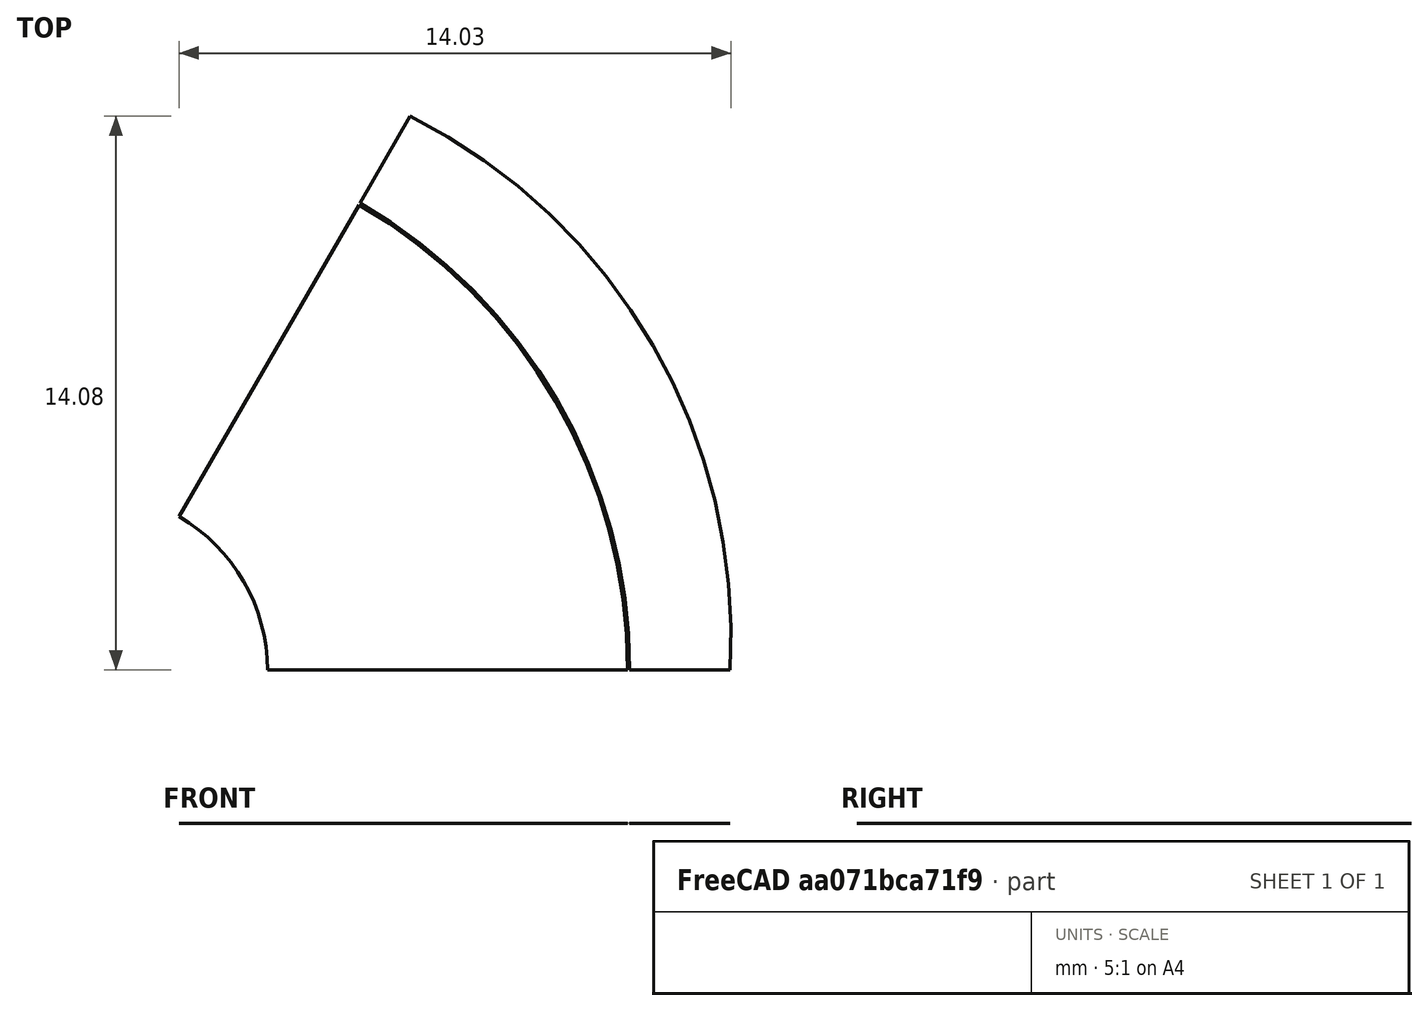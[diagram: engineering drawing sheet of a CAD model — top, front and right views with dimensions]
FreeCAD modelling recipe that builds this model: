
FCSTD DOCUMENT  (FreeCAD 0.18R4 (GitTag))
Label: RotorIRRingMagnet
License: All rights reserved
LicenseURL: http://en.wikipedia.org/wiki/All_rights_reserved
objects: Sketcher::SketchObject×5, PartDesign::Body×2, Surface::Filling×2, Spreadsheet::Sheet×1
note: 9 computed .brp shape members not serialized (recipe doc carries the construction recipe); baked Part::Feature solids carry a one-line shape summary decoded from their .brp

FEATURE [Spreadsheet::Sheet] Spreadsheet  label="Variables"
  cells = A2=poleNumber; B2(poleNumber)=6; A3=outerDiameter; B3(outerDiameter)=33; D3=Calc Value; A4=innerDiameter; B4(innerDiameter)=9; D4=Input Value; A5=stackLength; B5(stackLength)=20; A6=stackingFactor; B6(stackingFactor)=0.95; A7=embrace; B7(embrace)=75; A8=contourRatio; B8(contourRatio)=90; A9=magnetAirgap; B9(magnetAirgap)=0.05; A10=poleSeparation; B10(poleSeparation)=2; A11=magnetWidth; B11(magnetWidth)=9; A12=magnetHeight; B12(magnetHeight)=2.8; A13=rib; B13(rib)=0.5; A14=bridgeCurved; B14(bridgeCurved)=0.5; A15=cutTop; B15(cutTop)=0.2; A16=cutBottom; B16(cutBottom)=0.25; A17=segmentAngle; B17(segmentAngle)==360 / poleNumber; A18=movePocketInwards; B18(movePocketInwards)=0.5; A19=cuttingThickness; B19(cuttingThickness)=0.1; A20=magnetLength; B20(magnetLength)==stackLength; A21=cut; B21(cut)=0.2; A22=ribShaft; B22(ribShaft)=0.5; A23=magnetEmbrace; B23(magnetEmbrace)=70; A24=magnetContourRatio; B24(magnetContourRatio)=90; A25=axialMisalignment; B25(axialMisalignment)=0.5
FEATURE [Sketcher::SketchObject] Sketch003  label="RotorSketch"
  MapMode = 5
  Support = -> [XY_Plane]
  expr: Constraints[15] = Variables.outerDiameter / 2
  expr: Constraints[18] = Variables.segmentAngle / 2
  expr: Constraints[0] = Variables.segmentAngle
  expr: Constraints[27] = Variables.outerDiameter / 2 - Variables.magnetHeight - Variables.magnetAirgap
  expr: Constraints[14] = Variables.innerDiameter / 2
  expr: Constraints[23] = Variables.outerDiameter / 2 * Variables.contourRatio / 100
  sketch-geometry (11):
    g0: LineSegment [constr] StartX=4.5 StartY=0 StartZ=0 EndX=16.5 EndY=0 EndZ=0
    g1: LineSegment [constr] StartX=2.25 StartY=3.89711 StartZ=0 EndX=8.25 EndY=14.2894 EndZ=0
    g2: LineSegment [constr] StartX=0 StartY=0 StartZ=0 EndX=4.5 EndY=0 EndZ=0
    g3: LineSegment [constr] StartX=0 StartY=0 StartZ=0 EndX=2.25 EndY=3.89711 EndZ=0
    g4: ArcOfCircle [constr] CenterX=0 CenterY=0 CenterZ=0 NormalX=0 NormalY=0 NormalZ=1 AngleXU=0 Radius=16.5 StartAngle=0 EndAngle=1.0472
    g5: ArcOfCircle CenterX=0 CenterY=0 CenterZ=0 NormalX=0 NormalY=0 NormalZ=1 AngleXU=0 Radius=4.5 StartAngle=0 EndAngle=1.0472
    g6: LineSegment [constr] StartX=0 StartY=0 StartZ=0 EndX=14.2894 EndY=8.25 EndZ=0
    g7: ArcOfCircle [constr] CenterX=1.42894 CenterY=0.825 CenterZ=0 NormalX=0 NormalY=0 NormalZ=1 AngleXU=0 Radius=14.85 StartAngle=6.2276 EndAngle=7.38597
    g8: ArcOfCircle CenterX=0 CenterY=0 CenterZ=0 NormalX=0 NormalY=0 NormalZ=1 AngleXU=0 Radius=13.65 StartAngle=0 EndAngle=1.0472
    g9: LineSegment StartX=2.25 StartY=3.89711 StartZ=0 EndX=6.825 EndY=11.8212 EndZ=0
    g10: LineSegment StartX=4.5 StartY=0 StartZ=0 EndX=13.65 EndY=0 EndZ=0
  constraints (32):
    c: Angle(g0,g1) = 1.0472
    c: Coincident(g2,g-1)
    c: Coincident(g2,g0)
    c: Coincident(g3,g2)
    c: Coincident(g3,g1)
    c: Parallel(g2,g0)
    c: Parallel(g3,g1)
    c: Coincident(g4,g-1)
    c: Coincident(g4,g0)
    c: Coincident(g4,g1)
    c: Coincident(g5,g4)
    c: Coincident(g5,g1)
    c: Coincident(g5,g0)
    c: Angle(g-1,g2) = 0
    c: Radius(g5) = 4.5
    c: Radius(g4) = 16.5
    c: Coincident(g6,g5)
    c: PointOnObject(g6,g4)
    c: Angle(g-1,g6) = 0.523599
    c: PointOnObject(g7,g1)
    c: PointOnObject(g7,g0)
    c: PointOnObject(g6,g7)
    c: PointOnObject(g7,g6)
    c: Radius(g7) = 14.85
    c: Coincident(g8,g5)
    c: PointOnObject(g8,g1)
    c: PointOnObject(g8,g0)
    c: Radius(g8) = 13.65
    c: Coincident(g9,g5)
    c: Coincident(g9,g8)
    c: Coincident(g10,g5)
    c: Coincident(g10,g8)
FEATURE [Sketcher::SketchObject] Sketch004  label="BoundingBox"
  MapMode = 5
  Support = -> [XY_Plane]
  expr: Constraints[8] = Variables.outerDiameter
  sketch-geometry (6):
    g0: LineSegment StartX=-16.5 StartY=-16.5 StartZ=0 EndX=16.5 EndY=-16.5 EndZ=0
    g1: LineSegment StartX=16.5 StartY=-16.5 StartZ=0 EndX=16.5 EndY=16.5 EndZ=0
    g2: LineSegment StartX=16.5 StartY=16.5 StartZ=0 EndX=-16.5 EndY=16.5 EndZ=0
    g3: LineSegment StartX=-16.5 StartY=16.5 StartZ=0 EndX=-16.5 EndY=-16.5 EndZ=0
    g4: LineSegment [constr] StartX=-16.5 StartY=-16.5 StartZ=0 EndX=16.5 EndY=16.5 EndZ=0
    g5: GeomPoint X=0 Y=0 Z=0
  constraints (14):
    c: Coincident(g0,g1)
    c: Coincident(g1,g2)
    c: Coincident(g2,g3)
    c: Coincident(g3,g0)
    c: Horizontal(g0)
    c: Horizontal(g2)
    c: Vertical(g1)
    c: Vertical(g3)
    c: DistanceY(g1,g1) = 33
    c: Equal(g2,g1)
    c: Coincident(g4,g0)
    c: Coincident(g4,g1)
    c: Symmetric(g0,g1,g5)
    c: Coincident(g-1,g5)
FEATURE [Sketcher::SketchObject] Sketch005  label="RotorSideSketch"
  MapMode = 5
  Support = -> [XY_Plane001]
  expr: Constraints[22] = Variables.stackLength / 2 - Variables.axialMisalignment
  expr: Constraints[9] = Variables.outerDiameter / 2
  expr: Constraints[8] = Variables.innerDiameter / 2
  expr: Constraints[7] = Variables.stackLength
  sketch-geometry (8):
    g0: LineSegment StartX=-9.5 StartY=4.5 StartZ=0 EndX=10.5 EndY=4.5 EndZ=0
    g1: LineSegment StartX=10.5 StartY=4.5 StartZ=0 EndX=10.5 EndY=16.5 EndZ=0
    g2: LineSegment StartX=10.5 StartY=16.5 StartZ=0 EndX=-9.5 EndY=16.5 EndZ=0
    g3: LineSegment StartX=-9.5 StartY=16.5 StartZ=0 EndX=-9.5 EndY=4.5 EndZ=0
    g4: LineSegment StartX=-9.5 StartY=-4.5 StartZ=0 EndX=10.5 EndY=-4.5 EndZ=0
    g5: LineSegment StartX=10.5 StartY=-4.5 StartZ=0 EndX=10.5 EndY=-16.5 EndZ=0
    g6: LineSegment StartX=10.5 StartY=-16.5 StartZ=0 EndX=-9.5 EndY=-16.5 EndZ=0
    g7: LineSegment StartX=-9.5 StartY=-16.5 StartZ=0 EndX=-9.5 EndY=-4.5 EndZ=0
  constraints (23):
    c: Coincident(g0,g1)
    c: Coincident(g1,g2)
    c: Coincident(g2,g3)
    c: Coincident(g3,g0)
    c: Horizontal(g0)
    c: Vertical(g1)
    c: Vertical(g3)
    c: DistanceX(g2,g2) = 20
    c: DistanceY(g-1,g0) = 4.5
    c: DistanceY(g-1,g1) = 16.5
    c: Coincident(g4,g5)
    c: Coincident(g5,g6)
    c: Coincident(g6,g7)
    c: Coincident(g7,g4)
    c: Horizontal(g4)
    c: Vertical(g5)
    c: Vertical(g7)
    c: Equal(g4,g0)
    c: Equal(g7,g3)
    c: Horizontal(g6)
    c: Horizontal(g2)
    c: Symmetric(g4,g0,g-1)
    c: DistanceX(g0,g-1) = 9.5
FEATURE [Sketcher::SketchObject] Sketch006  label="MagnetSideSketch"
  ExternalGeometry = -> [Sketch005]
  MapMode = 5
  Support = -> [XY_Plane001]
  expr: Constraints[19] = Variables.stackLength / 2 - Variables.axialMisalignment
  expr: Constraints[7] = Variables.magnetHeight
  sketch-geometry (8):
    g0: LineSegment StartX=-9.5 StartY=13.7 StartZ=0 EndX=10.5 EndY=13.7 EndZ=0
    g1: LineSegment StartX=10.5 StartY=13.7 StartZ=0 EndX=10.5 EndY=16.5 EndZ=0
    g2: LineSegment StartX=10.5 StartY=16.5 StartZ=0 EndX=-9.5 EndY=16.5 EndZ=0
    g3: LineSegment StartX=-9.5 StartY=16.5 StartZ=0 EndX=-9.5 EndY=13.7 EndZ=0
    g4: LineSegment StartX=-9.5 StartY=-16.5 StartZ=0 EndX=10.5 EndY=-16.5 EndZ=0
    g5: LineSegment StartX=10.5 StartY=-16.5 StartZ=0 EndX=10.5 EndY=-13.7 EndZ=0
    g6: LineSegment StartX=10.5 StartY=-13.7 StartZ=0 EndX=-9.5 EndY=-13.7 EndZ=0
    g7: LineSegment StartX=-9.5 StartY=-13.7 StartZ=0 EndX=-9.5 EndY=-16.5 EndZ=0
  constraints (21):
    c: Coincident(g0,g1)
    c: Coincident(g1,g2)
    c: Coincident(g2,g3)
    c: Coincident(g3,g0)
    c: Horizontal(g0)
    c: Vertical(g1)
    c: Vertical(g3)
    c: DistanceY(g1,g1) = 2.8
    c: Coincident(g4,g5)
    c: Coincident(g5,g6)
    c: Coincident(g6,g7)
    c: Coincident(g7,g4)
    c: Horizontal(g4)
    c: Vertical(g5)
    c: Vertical(g7)
    c: Symmetric(g6,g0,g-1)
    c: Symmetric(g5,g0,g-1)
    c: Equal(g7,g3)
    c: Coincident(g1,g-3)
    c: DistanceX(g0,g-1) = 9.5
    c: Horizontal(g2)
FEATURE [PartDesign::Body] Body001  label="SideView"
  Group = -> [Sketch005,Sketch006]
  Origin = -> Origin001
FEATURE [Surface::Filling] Surface  label="Rotor_Surface"
  Anisotropy = false
  BoundaryEdges = -> [Sketch003]
  BoundaryOrder = [0,0,0,0]
  Degree = 3
  Iterations = 2
  MaximumDegree = 8
  MaximumSegments = 9
  PointsOnCurve = 15
  TolAngular = 0.01
  TolCurvature = 0.1
  Tolerance2d = 1e-05
  Tolerance3d = 0.0001
FEATURE [Sketcher::SketchObject] Sketch007  label="MagnetSketch"
  MapMode = 5
  Support = -> [XY_Plane]
  expr: Constraints[35] = Variables.outerDiameter / 2 - Variables.magnetHeight
  expr: Constraints[15] = Variables.outerDiameter / 2
  expr: Constraints[18] = Variables.segmentAngle / 2
  expr: Constraints[0] = Variables.segmentAngle
  expr: Constraints[27] = Variables.outerDiameter / 2 - Variables.magnetHeight - Variables.magnetAirgap
  expr: Constraints[14] = Variables.innerDiameter / 2
  expr: Constraints[23] = Variables.outerDiameter / 2 * Variables.magnetContourRatio / 100
  sketch-geometry (14):
    g0: LineSegment [constr] StartX=4.5 StartY=0 StartZ=0 EndX=16.5 EndY=0 EndZ=0
    g1: LineSegment [constr] StartX=2.25 StartY=3.89711 StartZ=0 EndX=8.25 EndY=14.2894 EndZ=0
    g2: LineSegment [constr] StartX=0 StartY=0 StartZ=0 EndX=4.5 EndY=0 EndZ=0
    g3: LineSegment [constr] StartX=0 StartY=0 StartZ=0 EndX=2.25 EndY=3.89711 EndZ=0
    g4: ArcOfCircle [constr] CenterX=0 CenterY=0 CenterZ=0 NormalX=0 NormalY=0 NormalZ=1 AngleXU=0 Radius=16.5 StartAngle=0 EndAngle=1.0472
    g5: ArcOfCircle [constr] CenterX=0 CenterY=0 CenterZ=0 NormalX=0 NormalY=0 NormalZ=1 AngleXU=0 Radius=4.5 StartAngle=0 EndAngle=1.0472
    g6: LineSegment [constr] StartX=0 StartY=0 StartZ=0 EndX=14.2894 EndY=8.25 EndZ=0
    g7: ArcOfCircle CenterX=1.42894 CenterY=0.825 CenterZ=0 NormalX=0 NormalY=0 NormalZ=1 AngleXU=0 Radius=14.85 StartAngle=6.2276 EndAngle=7.38597
    g8: ArcOfCircle [constr] CenterX=0 CenterY=0 CenterZ=0 NormalX=0 NormalY=0 NormalZ=1 AngleXU=0 Radius=13.65 StartAngle=0 EndAngle=1.0472
    g9: LineSegment [constr] StartX=2.25 StartY=3.89711 StartZ=0 EndX=6.825 EndY=11.8212 EndZ=0
    g10: LineSegment [constr] StartX=4.5 StartY=0 StartZ=0 EndX=13.65 EndY=0 EndZ=0
    g11: ArcOfCircle CenterX=0 CenterY=0 CenterZ=0 NormalX=0 NormalY=0 NormalZ=1 AngleXU=0 Radius=13.7 StartAngle=0 EndAngle=1.0472
    g12: LineSegment StartX=6.85 StartY=11.8645 StartZ=0 EndX=8.128 EndY=14.0781 EndZ=0
    g13: LineSegment StartX=13.7 StartY=0 StartZ=0 EndX=16.256 EndY=0 EndZ=0
  constraints (40):
    c: Angle(g0,g1) = 1.0472
    c: Coincident(g2,g-1)
    c: Coincident(g2,g0)
    c: Coincident(g3,g2)
    c: Coincident(g3,g1)
    c: Parallel(g2,g0)
    c: Parallel(g3,g1)
    c: Coincident(g4,g-1)
    c: Coincident(g4,g0)
    c: Coincident(g4,g1)
    c: Coincident(g5,g4)
    c: Coincident(g5,g1)
    c: Coincident(g5,g0)
    c: Angle(g-1,g2) = 0
    c: Radius(g5) = 4.5
    c: Radius(g4) = 16.5
    c: Coincident(g6,g5)
    c: PointOnObject(g6,g4)
    c: Angle(g-1,g6) = 0.523599
    c: PointOnObject(g7,g1)
    c: PointOnObject(g7,g0)
    c: PointOnObject(g6,g7)
    c: PointOnObject(g7,g6)
    c: Radius(g7) = 14.85
    c: Coincident(g8,g5)
    c: PointOnObject(g8,g1)
    c: PointOnObject(g8,g0)
    c: Radius(g8) = 13.65
    c: Coincident(g9,g5)
    c: Coincident(g9,g8)
    c: Coincident(g10,g5)
    c: Coincident(g10,g8)
    c: Coincident(g11,g-1)
    c: PointOnObject(g11,g1)
    c: PointOnObject(g11,g0)
    c: Radius(g11) = 13.7
    c: Coincident(g12,g11)
    c: Coincident(g12,g7)
    c: Coincident(g13,g11)
    c: Coincident(g13,g7)
FEATURE [PartDesign::Body] Body  label="TopView"
  Group = -> [Sketch003,Sketch004,Sketch007]
  Origin = -> Origin
FEATURE [Surface::Filling] Surface001  label="Magnet_Surface"
  Anisotropy = false
  BoundaryEdges = -> [Sketch007]
  BoundaryOrder = [0,0,0,0]
  Degree = 3
  Iterations = 2
  MaximumDegree = 8
  MaximumSegments = 9
  PointsOnCurve = 15
  TolAngular = 0.01
  TolCurvature = 0.1
  Tolerance2d = 1e-05
  Tolerance3d = 0.0001
